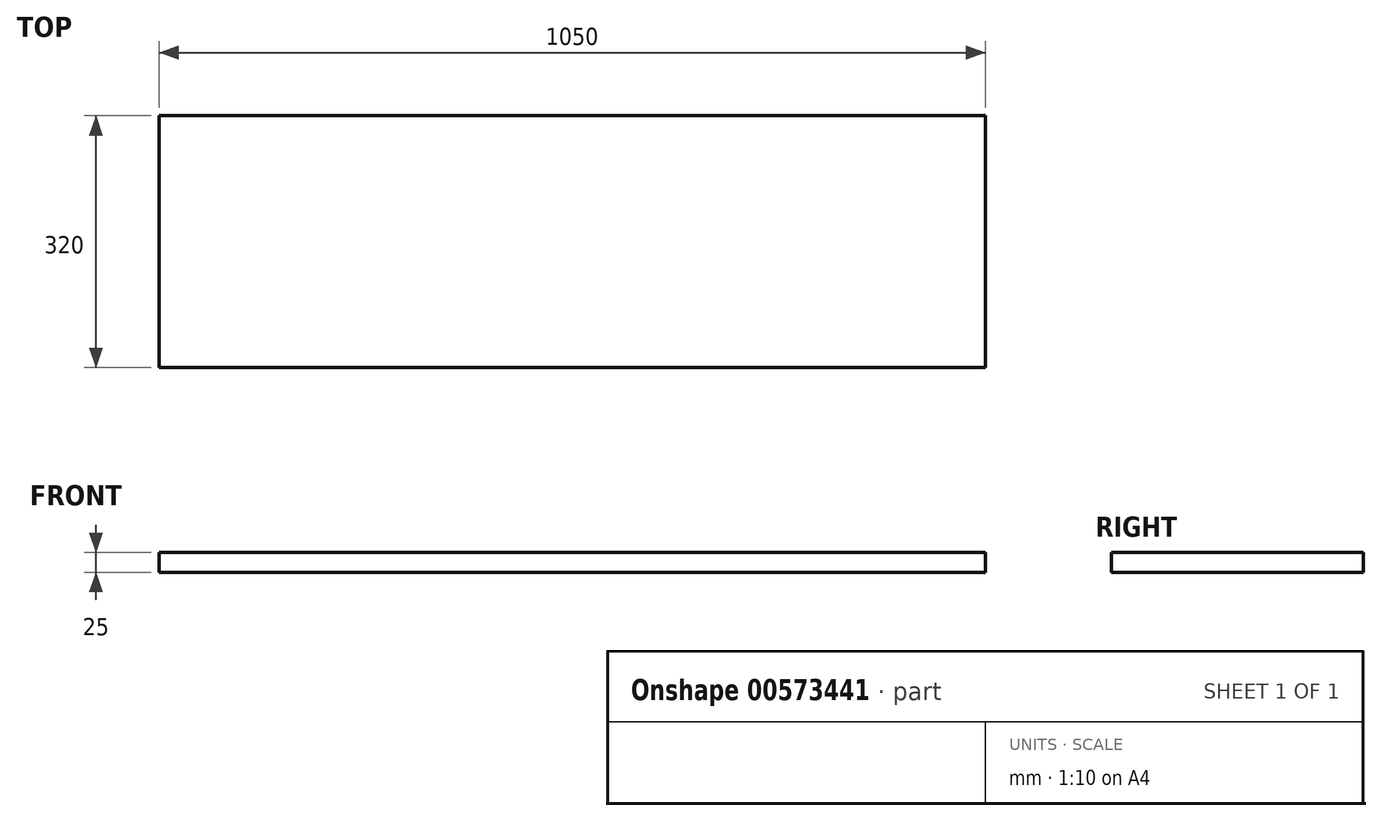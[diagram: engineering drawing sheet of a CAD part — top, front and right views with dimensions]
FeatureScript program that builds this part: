
annotation { "Feature Type Name" : "Feature", "Feature Type Description" : "" }
export const myFeature = defineFeature(function(context is Context, id is Id, definition is map)
    precondition{}
    {
        {
            var Q0;
            Q0=qCreatedBy(makeId("Top.planeOp"),FACE);
            var sketch = newSketch(context, id + "F0", { "sketchPlane" : qUnion([Q0])});
            skLineSegment(sketch, "E0.bottom", {"start": v(-194.4, 136.69) * mm, "end": v(855.6, 136.69) * mm});
            skLineSegment(sketch, "E0.top", {"start": v(-194.4, -183.31) * mm, "end": v(855.6, -183.31) * mm});
            skLineSegment(sketch, "E0.left", {"start": v(-194.4, 136.69) * mm, "end": v(-194.4, -183.31) * mm});
            skLineSegment(sketch, "E0.right", {"start": v(855.6, 136.69) * mm, "end": v(855.6, -183.31) * mm});
            skSolve(sketch);
        }
        {
            var Q0;
            Q0 = qSketchRegion(id + "F0", true);
            extrude(context, id + "F1", {"entities" : qUnion([Q0]), "depth" : 25 * mm, "offsetDistance" : 25 * mm});
        }
    });
